# Revit family: Lighting_Fixture-Lutron-Recessed-Finire-Prime-Square
name_source: partatom
category: Lighting Fixtures
revit_build: Autodesk Revit 2017 (Build: 20160720_1515(x64)
units: mm (PartAtom-declared; Revit-internal decimal feet)

## family parameters
Cut with Voids When Loaded = No
Host = Face
Light Source = Yes
OmniClass Number = 23.80.70.11.14
OmniClass Title = General Luminaries, Directional
Part Type = Normal
Room Calculation Point = No
Round Connector Dimension = Use Diameter
Shared = No

## types (4) — shared parameters
Apparent Load = 14 W
Assembly Code = D5020200
BIMobject category = Ceiling Mounted
Color Filter = 16777215
Connector Description = Power Connection
Date of publishing = 3/1/2017
Default Elevation = 25 "
Description = Finire Prime LED Square Recessed Downlight
Design country = United States
Dimming Lamp Color Temperature Shift = <None>
Edition number = 1
Finish = Metal - Lutron - MW - Matte White
Frame Finish = Steel - Lutron - 20 Gauge
IFC Classification = Light Fixture
Instruction Sheet Link = http://www.lutron.com
Keynote = 26 51 00
Lamp = LED
Load Classification = Lighting
Manufacturer = Lutron Electronics Co., Inc
Manufacturer Fax Number = 610-282-1243
Manufacturer country = Canada
Manufacturer name = Lutron Electronics
Material main = Aluminium
Model = See Housing and Trim Model Information
NBS Reference Code = 49
NBS Reference Description = Luminaires And Lamps
Nominal height = 3 "
Nominal width = 4.95 "
Number of Light Sources = 1
Number of Poles = 1
OmniClass Code = 23-35 47 11
OmniClass Description = Lighting Fixtures
Parameter Adjustment = Editing parameter values for type properties is not recommended as you may choose options that are not available.
Performance URL = http://www.lutron.com
Power Factor = 1
Product Documentation Link = http://www.lutron.com
Product Name = Finiré Prime Square
Product Page URL = http://www.lutron.com
Product SKU = lutron-finire-prime
Product family = General Luminaries, Directional
Product group = Ivalo Collection
Series = Finiré Prime, Adjustable, Trimmed
Tilt Angle = 0.00°
UNSPSC Code = 3911
URL = http://www.lutron.com
Uniclass 1.4 Code = L74
Uniclass 1.4 Description = Electric power and lighting services products
Uniclass 2.0 Code = PR-49
Uniclass 2.0 Description = Luminaires And Lamps
Version = 2017 - v1.0b
Video Link = https://www.youtube.com
Voltage = 120 V
Warranty URL = http://www.lutron.com
Wattage Comments = 14
Weight Net (Kg) = 2
zero-valued in all types: Cost

## per-type parameters (varying)
| type | Beam Spread | Constraint | LED | Photometric Web File |
| 2700K_30 Degree | 30.00° | 1 | 2700K 14W 1000 lumens 90+ CRI | Finire Prime RD 27K 30° - FPATR27X30MW.ies |
| 2700K_65 Degree | 65.00° | 2 | 2700K 14W 1000 lumens 90+ CRI | Finire Prime RD 27K 65° - FPATR27X65MW.ies |
| 3000K_30 Degree | 30.00° | 3 | 3000K 14W 1000 lumens 90+ CRI | Finire Prime RD 27K 30° - FPATR27X30MW.ies |
| 3000K_65 Degree | 65.00° | 4 | 3000K 14W 1000 lumens 90+ CRI | Finire Prime RD 27K 65° - FPATR27X65MW.ies |

## geometry (parser evidence)
native form markers: Sweep x4
no freeform markers — native parametric forms only
